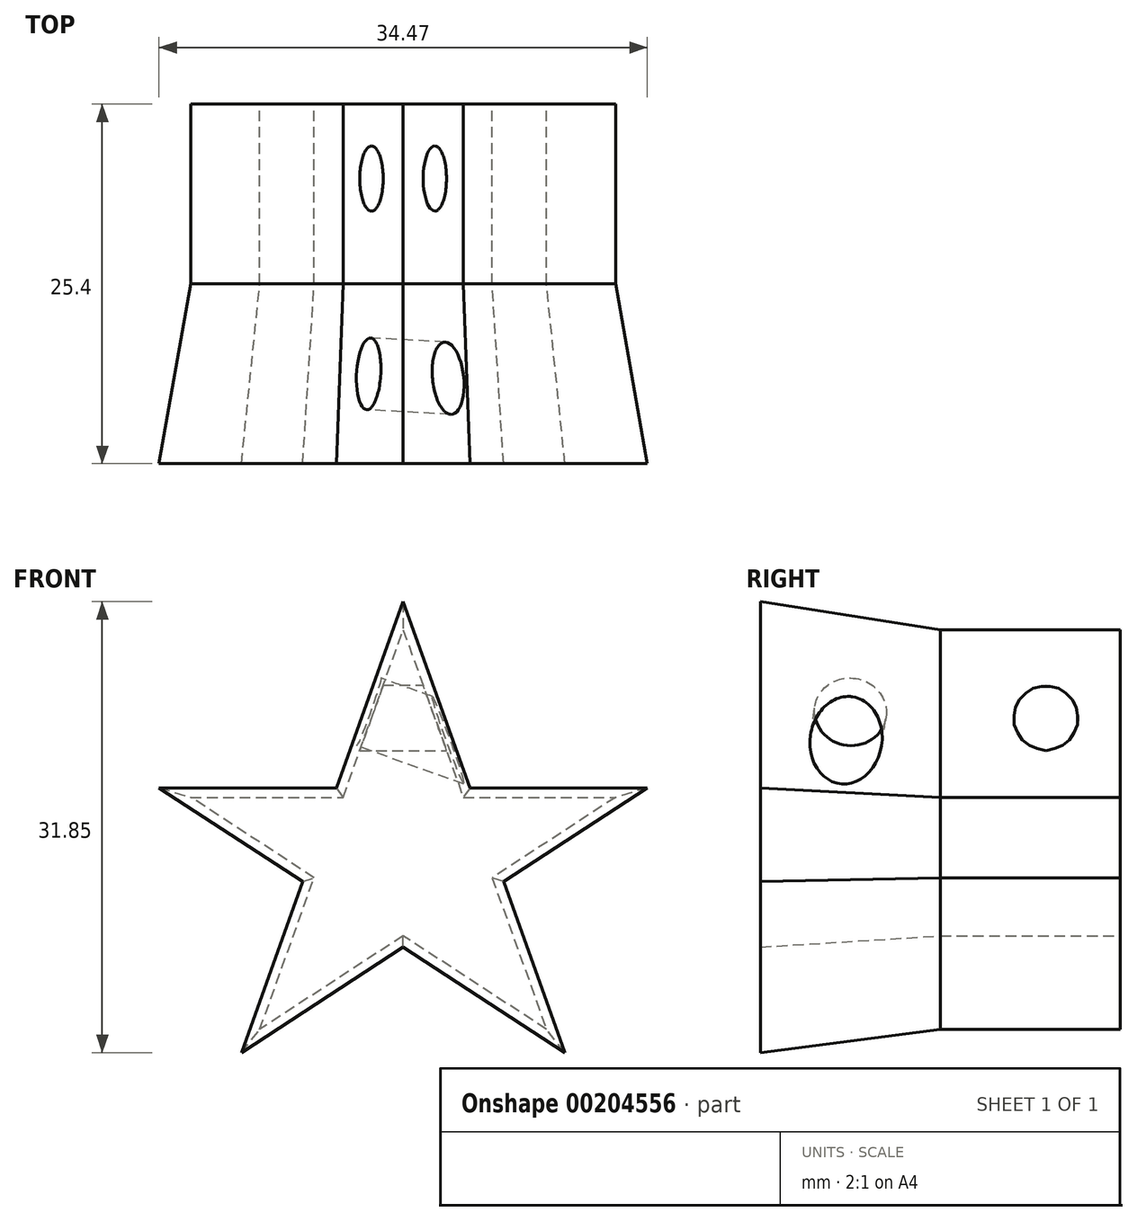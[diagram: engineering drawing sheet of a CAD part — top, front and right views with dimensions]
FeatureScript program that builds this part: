
annotation { "Feature Type Name" : "Feature", "Feature Type Description" : "" }
export const myFeature = defineFeature(function(context is Context, id is Id, definition is map)
    precondition{}
    {
        {
            var Q0;
            Q0=qCreatedBy(makeId("Front.planeOp"),FACE);
            var sketch = newSketch(context, id + "F0", { "sketchPlane" : qUnion([Q0])});
            skLineSegment(sketch, "E0", {"start": v(-21.34, -2.5) * mm, "end": v(-7.72, 53.55) * mm});
            skLineSegment(sketch, "E1", {"start": v(-7.72, 53.55) * mm, "end": v(5.9, -2.5) * mm});
            skLineSegment(sketch, "E2", {"start": v(5.9, -2.5) * mm, "end": v(-36.56, 36.54) * mm});
            skLineSegment(sketch, "E3", {"start": v(-36.56, 36.54) * mm, "end": v(21.12, 36.54) * mm});
            skLineSegment(sketch, "E4", {"start": v(21.12, 36.54) * mm, "end": v(-21.34, -2.5) * mm});
            skPoint(sketch, "E5", {"position": v(-7.72, 10.02) * mm});
            skSolve(sketch);
        }
        {
            var Q0;
            Q0=qCreatedBy(makeId("Front.planeOp"),FACE);
            var sketch = newSketch(context, id + "F1", { "sketchPlane" : qUnion([Q0])});
            skLineSegment(sketch, "E6", {"start": v(-20.25, 0) * mm, "end": v(-10.12, 28.24) * mm});
            skLineSegment(sketch, "E7", {"start": v(-10.12, 28.24) * mm, "end": v(0, 0) * mm});
            skLineSegment(sketch, "E8", {"start": v(0, 0) * mm, "end": v(-25.12, 16.4) * mm});
            skLineSegment(sketch, "E9", {"start": v(-25.12, 16.4) * mm, "end": v(4.88, 16.4) * mm});
            skLineSegment(sketch, "E10", {"start": v(4.88, 16.4) * mm, "end": v(-20.25, 0) * mm});
            skPoint(sketch, "E11", {"position": v(-10.12, 6.6) * mm});
            skPoint(sketch, "E12", {"position": v(-5.88, 16.4) * mm});
            skSolve(sketch);
        }
        {
            var Q0;
            Q0 = qSketchRegion(id + "F1", true);
            extrude(context, id + "F2", {"entities" : qUnion([Q0]), "depth" : 12.7 * mm, "hasDraft" : true, "draftAngle" : 3 * degree, "hasSecondDirection" : true, "secondDirectionOppositeDirection" : true, "secondDirectionDepth" : 12.7 * mm});
        }
        {
            var Q0;
            {var subQ0=sQuery(id+"F1.wireOp",EDGE,"E6");Q0=makeQuery(id+"F2.*.split.splitOp","SPLIT",FACE,{"derivedFrom":makeQuery(id+"F2.opExtrude","SWEPT_FACE",FACE,{"disambiguationData":[OSD([subQ0]),TDD([makeQuery(id+"F1.imprint","IMPRINT",EDGE,{"disambiguationData":[TD([[makeQuery(id+"F1.imprint","INTERSECT",VERTEX,{"derivedFrom":[subQ0,sQuery(id+"F1.wireOp",EDGE,"E7")]}),1.0]])],"derivedFrom":subQ0})])]})});}
            var sketch = newSketch(context, id + "F3", { "sketchPlane" : qUnion([Q0])});
            skCircle(sketch, "E13", {"center": v(7.36, 16.88) * mm, "radius": 2.54 * mm});
            skPoint(sketch, "E14", {"position": v(1, 16.88) * mm});
            skPoint(sketch, "E15", {"position": v(7.36, 24.1) * mm});
            skSolve(sketch);
        }
        {
            var Q0;
            Q0 = qSketchRegion(id + "F3", true);
            var Q1;
            Q1=sQuery(id+"F3.wireOp",EDGE,"E13");
            extrude(context, id + "F4", {"entities" : qUnion([Q0]), "operationType" : NewBodyOperationType.REMOVE, "surfaceEntities" : qUnion([Q1]), "endBound" : BoundingType.UP_TO_NEXT, "oppositeDirection" : true, "depth" : 25.4 * mm});
        }
        {
            var Q0;
            Q0=qCreatedBy(makeId("Right.planeOp"),FACE);
            var sketch = newSketch(context, id + "F5", { "sketchPlane" : qUnion([Q0])});
            skCircle(sketch, "E16", {"center": v(7.45, 22) * mm, "radius": 2.3 * mm});
            skSolve(sketch);
        }
        {
            var Q0;
            Q0 = qSketchRegion(id + "F5", true);
            extrude(context, id + "F6", {"entities" : qUnion([Q0]), "operationType" : NewBodyOperationType.REMOVE, "endBound" : BoundingType.THROUGH_ALL, "oppositeDirection" : true, "depth" : 25.4 * mm});
        }
    });
